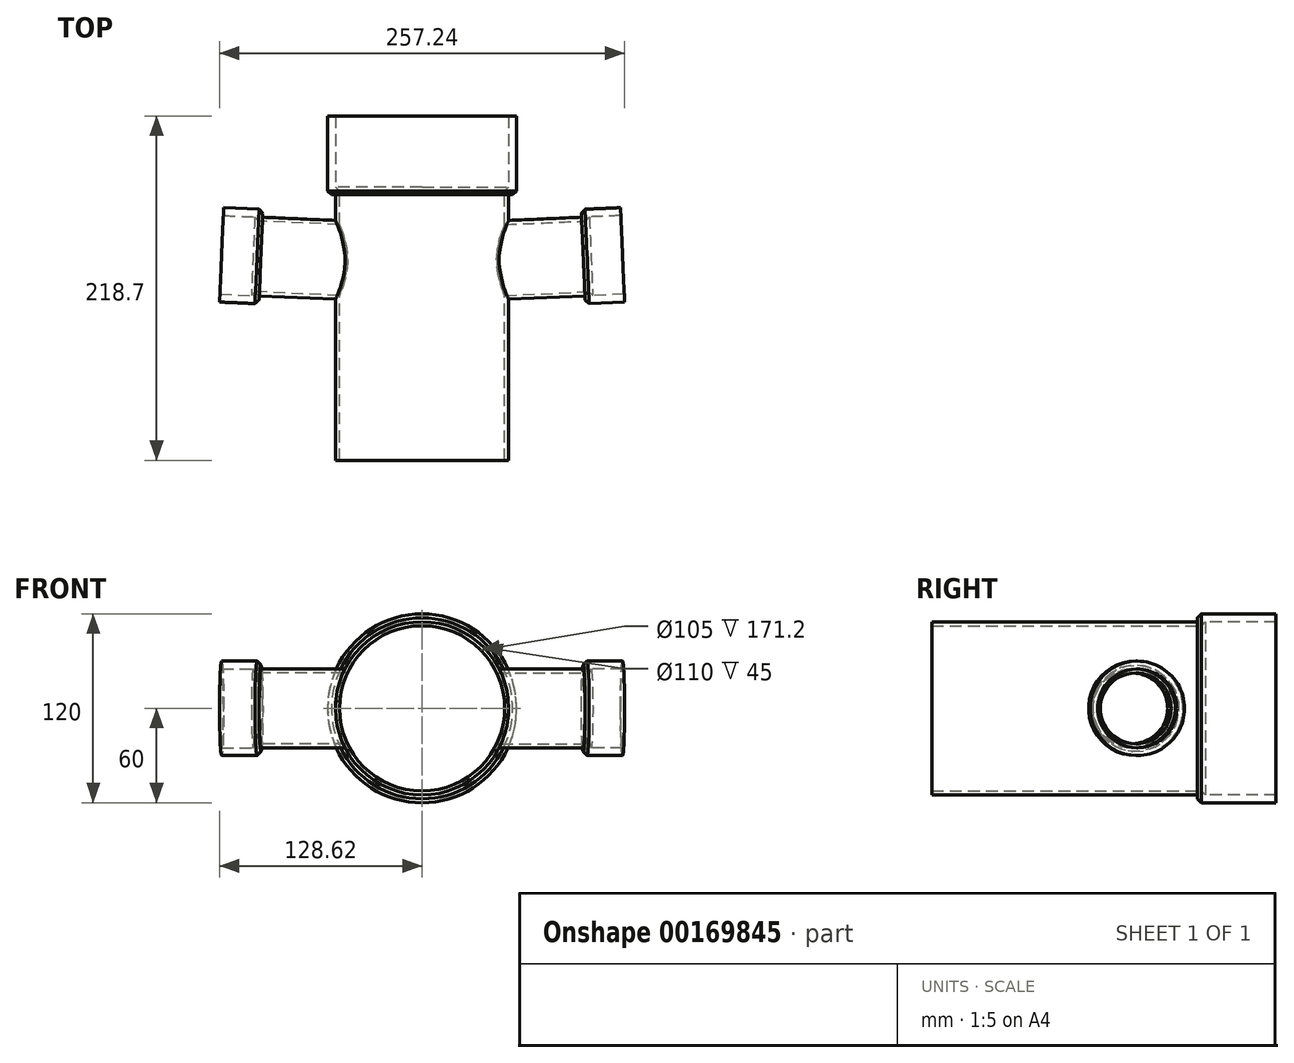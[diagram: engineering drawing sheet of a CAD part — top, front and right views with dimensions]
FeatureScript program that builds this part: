
annotation { "Feature Type Name" : "Feature", "Feature Type Description" : "" }
export const myFeature = defineFeature(function(context is Context, id is Id, definition is map)
    precondition{}
    {
        {
            var Q0;
            Q0=qCreatedBy(makeId("Top.planeOp"),FACE);
            var sketch = newSketch(context, id + "F0", { "sketchPlane" : qUnion([Q0])});
            skLineSegment(sketch, "E0", {"start": v(0, 0) * mm, "end": v(0, 168.7) * mm});
            skLineSegment(sketch, "E1", {"start": v(0, 125) * mm, "end": v(102.34, 129.47) * mm});
            skSolve(sketch);
        }
        {
            var Q0;
            Q0=sQuery(id+"F0.wireOp",EDGE,"E1");
            var Q1;
            Q1=sQuery(id+"F0.wireOp",VERTEX,"E1.start");
            cPlane(context, id + "F1", {"entities" : qUnion([Q0, Q1]), "cplaneType" : CPlaneType.LINE_POINT, "offset" : 25 * mm, "width" : 150 * mm, "height" : 150 * mm});
        }
        {
            var Q0;
            Q0=qCreatedBy(id+"F1.planeOp",FACE);
            var sketch = newSketch(context, id + "F2", { "sketchPlane" : qUnion([Q0])});
            skCircle(sketch, "E2", {"center": v(124.88, 0) * mm, "radius": 25 * mm});
            skSolve(sketch);
        }
        {
            var Q0;
            Q0=makeQuery(id+"F2.imprint","IMPRINT",FACE,{"disambiguationData":[TD([[makeQuery(id+"F2.imprint","IMPRINT",EDGE,{"derivedFrom":sQuery(id+"F2.wireOp",EDGE,"E2")}),1.0]])]});
            var Q1;
            Q1=sQuery(id+"F0.wireOp",EDGE,"E1");
            sweep(context, id + "F3", {"profiles" : qUnion([Q0]), "path" : qUnion([Q1])});
        }
        {
            var Q0;
            Q0=makeQuery(id+"F3.opSweep","SWEPT_BODY",BODY,{"disambiguationData":[OSD([sQuery(id+"F0.wireOp",EDGE,"E1"),sQuery(id+"F2.wireOp",EDGE,"E2")])]});
            var Q1;
            Q1=qCreatedBy(makeId("Right.planeOp"),FACE);
            mirror(context, id + "F4", {"operationType" : NewBodyOperationType.ADD, "entities" : qUnion([Q0]), "mirrorPlane" : qUnion([Q1])});
        }
        {
            var Q0;
            Q0=qCreatedBy(makeId("Front.planeOp"),FACE);
            var sketch = newSketch(context, id + "F5", { "sketchPlane" : qUnion([Q0])});
            skCircle(sketch, "E3", {"center": v(0, 0) * mm, "radius": 55 * mm});
            skSolve(sketch);
        }
        {
            var Q0;
            Q0=makeQuery(id+"F5.imprint","IMPRINT",FACE,{"disambiguationData":[TD([[makeQuery(id+"F5.imprint","IMPRINT",EDGE,{"derivedFrom":sQuery(id+"F5.wireOp",EDGE,"E3")}),1.0]])]});
            var Q1;
            Q1=sQuery(id+"F0.wireOp",EDGE,"E0");
            sweep(context, id + "F6", {"operationType" : NewBodyOperationType.ADD, "profiles" : qUnion([Q0]), "path" : qUnion([Q1])});
        }
        {
            var Q0;
            Q0=makeQuery(id+"F6.opSweep","CAP_FACE",FACE,{"disambiguationData":[OSD([sQuery(id+"F0.wireOp",VERTEX,"E0.start"),sQuery(id+"F5.wireOp",EDGE,"E3")])],"isStart":true});
            var Q1;
            Q1=makeQuery(id+"F3.opSweep","CAP_FACE",FACE,{"disambiguationData":[OSD([sQuery(id+"F0.wireOp",VERTEX,"E1.end"),sQuery(id+"F2.wireOp",EDGE,"E2")])],"isStart":false});
            var Q2;
            Q2=makeQuery(id+"F6.opSweep","CAP_FACE",FACE,{"disambiguationData":[OSD([sQuery(id+"F0.wireOp",VERTEX,"E0.end"),sQuery(id+"F5.wireOp",EDGE,"E3")])],"isStart":false});
            var Q3;
            Q3=makeQuery(id+"F4.opPattern","COPY",FACE,{"derivedFrom":makeQuery(id+"F3.opSweep","CAP_FACE",FACE,{"disambiguationData":[OSD([sQuery(id+"F0.wireOp",VERTEX,"E1.end"),sQuery(id+"F2.wireOp",EDGE,"E2")])],"isStart":false}),"instanceName":"1"});
            shell(context, id + "F7", {"entities" : qUnion([Q0, Q1, Q2, Q3]), "thickness" : 2.5 * mm});
        }
        {
            var Q0;
            Q0=makeQuery(id+"F6.opSweep","CAP_FACE",FACE,{"disambiguationData":[OSD([sQuery(id+"F0.wireOp",VERTEX,"E0.end"),sQuery(id+"F5.wireOp",EDGE,"E3")])],"isStart":false});
            var sketch = newSketch(context, id + "F8", { "sketchPlane" : qUnion([Q0])});
            skCircle(sketch, "E4.0", {"center": v(0, 0) * mm, "radius": 55 * mm});
            skCircle(sketch, "E5.0", {"center": v(0, 0) * mm, "radius": 60 * mm});
            skSolve(sketch);
        }
        {
            var Q0;
            Q0=makeQuery(id+"F8.imprint","IMPRINT",FACE,{"disambiguationData":[TD([[makeQuery(id+"F8.imprint","IMPRINT",EDGE,{"derivedFrom":sQuery(id+"F8.wireOp",EDGE,"E4.0")}),1.0]])]});
            extrude(context, id + "F9", {"entities" : qUnion([Q0]), "operationType" : NewBodyOperationType.ADD, "depth" : 5 * mm});
        }
        {
            var Q0;
            Q0 = qSketchRegion(id + "F8", true);
            extrude(context, id + "F10", {"entities" : qUnion([Q0]), "operationType" : NewBodyOperationType.ADD, "depth" : 50 * mm});
        }
        {
            var Q0;
            Q0=makeQuery(id+"F3.opSweep","CAP_FACE",FACE,{"disambiguationData":[OSD([sQuery(id+"F0.wireOp",VERTEX,"E1.end"),sQuery(id+"F2.wireOp",EDGE,"E2")])],"isStart":false});
            var sketch = newSketch(context, id + "F11", { "sketchPlane" : qUnion([Q0])});
            skCircle(sketch, "E6.0", {"center": v(124.88, 0) * mm, "radius": 25 * mm});
            skCircle(sketch, "E7.0", {"center": v(124.88, 0) * mm, "radius": 30 * mm});
            skSolve(sketch);
        }
        {
            var Q0;
            Q0=makeQuery(id+"F11.imprint","IMPRINT",FACE,{"disambiguationData":[TD([[makeQuery(id+"F11.imprint","IMPRINT",EDGE,{"derivedFrom":sQuery(id+"F11.wireOp",EDGE,"E6.0")}),1.0]])]});
            extrude(context, id + "F12", {"entities" : qUnion([Q0]), "operationType" : NewBodyOperationType.ADD, "depth" : 5 * mm});
        }
        {
            var Q0;
            Q0 = qSketchRegion(id + "F11", true);
            extrude(context, id + "F13", {"entities" : qUnion([Q0]), "operationType" : NewBodyOperationType.ADD, "depth" : 25 * mm});
        }
        {
            var Q0;
            Q0=makeQuery(id+"F4.opPattern","COPY",FACE,{"derivedFrom":makeQuery(id+"F3.opSweep","CAP_FACE",FACE,{"disambiguationData":[OSD([sQuery(id+"F0.wireOp",VERTEX,"E1.end"),sQuery(id+"F2.wireOp",EDGE,"E2")])],"isStart":false}),"instanceName":"1"});
            var sketch = newSketch(context, id + "F14", { "sketchPlane" : qUnion([Q0])});
            skCircle(sketch, "E8.0", {"center": v(-124.88, 0) * mm, "radius": 25 * mm});
            skCircle(sketch, "E9.0", {"center": v(-124.88, 0) * mm, "radius": 30 * mm});
            skSolve(sketch);
        }
        {
            var Q0;
            Q0=makeQuery(id+"F14.imprint","IMPRINT",FACE,{"disambiguationData":[TD([[makeQuery(id+"F14.imprint","IMPRINT",EDGE,{"derivedFrom":sQuery(id+"F14.wireOp",EDGE,"E8.0")}),-1.0]])]});
            extrude(context, id + "F15", {"entities" : qUnion([Q0]), "operationType" : NewBodyOperationType.ADD, "depth" : 5 * mm});
        }
        {
            var Q0;
            Q0 = qSketchRegion(id + "F14", true);
            extrude(context, id + "F16", {"entities" : qUnion([Q0]), "operationType" : NewBodyOperationType.ADD, "depth" : 25 * mm});
        }
        {
            var Q0;
            Q0=makeQuery(id+"F9.opExtrude","CAP_EDGE",EDGE,{"disambiguationData":[OSD([sQuery(id+"F0.wireOp",VERTEX,"E0.end"),sQuery(id+"F5.wireOp",EDGE,"E3")])],"isStart":false});
            var Q1;
            Q1=makeQuery(id+"F10.opExtrude","CAP_EDGE",EDGE,{"disambiguationData":[OSD([sQuery(id+"F8.wireOp",EDGE,"E5.0")])],"isStart":true});
            var Q2;
            Q2=makeQuery(id+"F16.opExtrude","CAP_EDGE",EDGE,{"disambiguationData":[OSD([sQuery(id+"F14.wireOp",EDGE,"E9.0")])],"isStart":true});
            var Q3;
            Q3=makeQuery(id+"F13.opExtrude","CAP_EDGE",EDGE,{"disambiguationData":[OSD([sQuery(id+"F11.wireOp",EDGE,"E7.0")])],"isStart":true});
            var Q4;
            Q4=makeQuery(id+"F12.opExtrude","CAP_EDGE",EDGE,{"disambiguationData":[OSD([sQuery(id+"F0.wireOp",VERTEX,"E1.end"),sQuery(id+"F2.wireOp",EDGE,"E2")])],"isStart":false});
            var Q5;
            Q5=makeQuery(id+"F15.opExtrude","CAP_EDGE",EDGE,{"disambiguationData":[OSD([sQuery(id+"F0.wireOp",VERTEX,"E1.end"),sQuery(id+"F2.wireOp",EDGE,"E2")])],"isStart":false});
            chamfer(context, id + "F17", {"entities" : qUnion([Q0, Q1, Q2, Q3, Q4, Q5]), "width" : 2.5 * mm, "tangentPropagation" : true});
        }
    });
